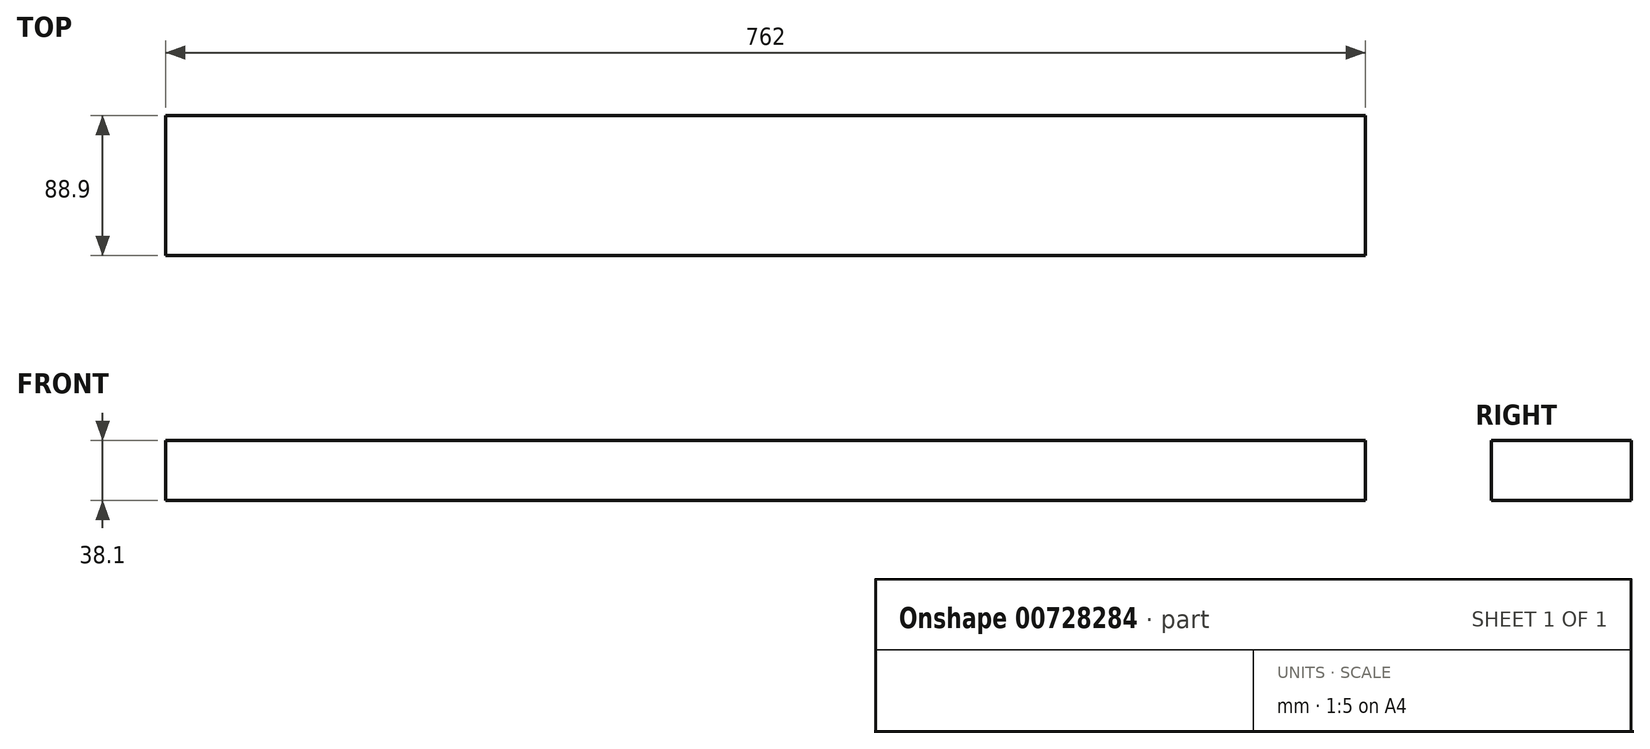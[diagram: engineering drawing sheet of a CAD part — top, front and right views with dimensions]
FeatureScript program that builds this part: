
annotation { "Feature Type Name" : "Feature", "Feature Type Description" : "" }
export const myFeature = defineFeature(function(context is Context, id is Id, definition is map)
    precondition{}
    {
        {
            var Q0;
            Q0=qCreatedBy(makeId("Front.planeOp"),FACE);
            var sketch = newSketch(context, id + "F0", { "sketchPlane" : qUnion([Q0])});
            skLineSegment(sketch, "E0.bottom", {"start": v(-381, -19.05) * mm, "end": v(381, -19.05) * mm});
            skLineSegment(sketch, "E0.top", {"start": v(-381, 19.05) * mm, "end": v(381, 19.05) * mm});
            skLineSegment(sketch, "E0.left", {"start": v(-381, -19.05) * mm, "end": v(-381, 19.05) * mm});
            skLineSegment(sketch, "E0.right", {"start": v(381, -19.05) * mm, "end": v(381, 19.05) * mm});
            skPoint(sketch, "E0.middle", {"position": v(0, 0) * mm});
            skSolve(sketch);
        }
        {
            var Q0;
            Q0=qSketchRegion(id+"F0",true);
            extrude(context, id + "F1", {"entities" : qUnion([Q0]), "depth" : 88.9 * mm, "offsetDistance" : 25.4 * mm});
        }
    });
